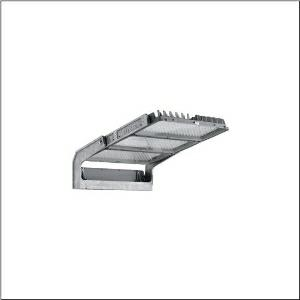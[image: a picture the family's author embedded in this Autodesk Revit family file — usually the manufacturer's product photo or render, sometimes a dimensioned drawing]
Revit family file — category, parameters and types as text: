
# Revit family: floodlight_fl_11_maxi_pro___rs08_5xa779228l01gb_a1ed
name_source: partatom
category: Lighting Fixtures
units: mm (PartAtom-declared; Revit-internal decimal feet)

## family parameters
Cut with Voids When Loaded = No
Host = Face
Light Source = No
Part Type = Normal
Room Calculation Point = No
Round Connector Dimension = Use Diameter
Shared = No

## types (1)
- --- (1 x LED, 148170 lm, 1285.1 W, 5700K)
    Apparent Load = 1285 VA
    CIE Flux Codes = 70 87 98 100 100
    Color Rendering = 80
    Color Temperature = 5700K
    Default Elevation = 1800 mm
    Description = Floodlight FL 11  maxi  pro floodlight; light control with lens of PMMA; cover panel of toughened safety glass, transparent; light distribution: RS08, rotationally symmetric direct distribution, LEDcolour temperature: 5700K, rated luminous flux: 148.170lm, colour rendering: CRI > 80, light colour: 857; luminous efficacy: 115lm/W; brightness control: DMX+RDM; with terminal, 6-pole, max. 2.5mm², mains connection: 220..240V/380..400V AC, 50/60Hz, surge voltage resistance: line to ground: 10kV, service life up to 100,000h L90. Typical operating time: 1000h per year, ECG replaceable separately, LED unit replaceable without ESD environment, dustproof LED module, dimming range 10..100%; 1285W floodlight with 3x LED unit of diecast aluminium, coated grey; length: 1.003mm / width: 651mm / height: 338mm; mounting bracket, of diecast aluminium, uncoated, natural, protection rating (complete): IP66; insulation class (complete): insulation class I (protective earthing); certification: CE, ENEC, VDE; ball protection: ball impact resistant, only for outdoor installations in the designated locations, permissible operating ambient temperature: -45..+55°C, permissible storage temperature: -40..+85°Cpackaging unit: 1 piece

Light Distribution: RS08
    Height = 320 mm
    Lamp = 1 x LED
    Lamp Light Flux = 148170 lm
    Lamp Power = 1285.1 W
    Lamp count = 1
    Length = 1002 mm
    Luminous efficacy = 115 lm/W
    Manufacturer = Siteco
    ModVariant = No
    Model = 5XA779228L01GB
    Mounting Place = Ceiling
    Mounting Type = Surface mounted
    Number of Poles = 1
    OnlyDefault = Yes
    Power Factor = 1
    Product Name = Floodlight FL 11 maxi pro | RS08
    Product group = floodlight | ceiling mounted
    ProductGroupID = 301
    Protection Class = Protection class I
    Protection Degree = IP 66
    RLX_Detail_Level = 1
    RLX_Emergency_Light_Flux = 0 lm
    RLX_Emergency_Type = 0
    RLX_Emergency_Type_DB = No
    RlxData = <blob elided: 40385 chars, md5=29ab8674>
    Socket = socket
    Standby Power = 0 W
    System Light Flux = 148170 lm
    System Power = 1285 W
    Type Comments = factory setting: luminous flux: 100 % | dim-lin: 255 | 875 mA
    Type Image = l_1356210.jpg
    URL = http://relux.com
    VarID = @adj_014259
    Voltage = 0 V
    Weight = 0.00 kg
    Width = 655 mm

## geometry (parser evidence)
native form markers: Blend x4, Sweep x12
no freeform markers — native parametric forms only
